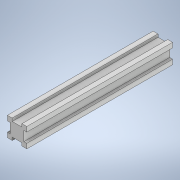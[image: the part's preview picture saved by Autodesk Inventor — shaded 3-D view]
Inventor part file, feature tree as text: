
AUTODESK INVENTOR PART (.ipt)
format: ipt  version: 2021 (Build 250183000, 183)  size: 126,464 bytes
history: native  units: mm
features: other x1, extrude x1, sketch x1
ambient origin geometry x8: Origin, YZ Plane, XZ Plane, XY Plane, X Axis, Y Axis, Z Axis, Center Point
bodies: Body1 (feature_tree)
feature tree (3):
  other  "Sólido1"
  extrude  "Extrusão1"  Depth=5.0mm
  sketch  "Esboço1"  dims[d4=5.0mm d5=5.0mm d6=3.0mm d7=10.0mm d8=3.0mm d9=5.0mm d10=5.0mm d11=3.0mm d12=10.0mm d13=5.0mm d14=5.0mm d15=3.0mm d16=10.0mm d17=3.0mm d18=5.0mm d19=3.0mm d20=10.0mm d21=150.0mm d22=0.0mm]
